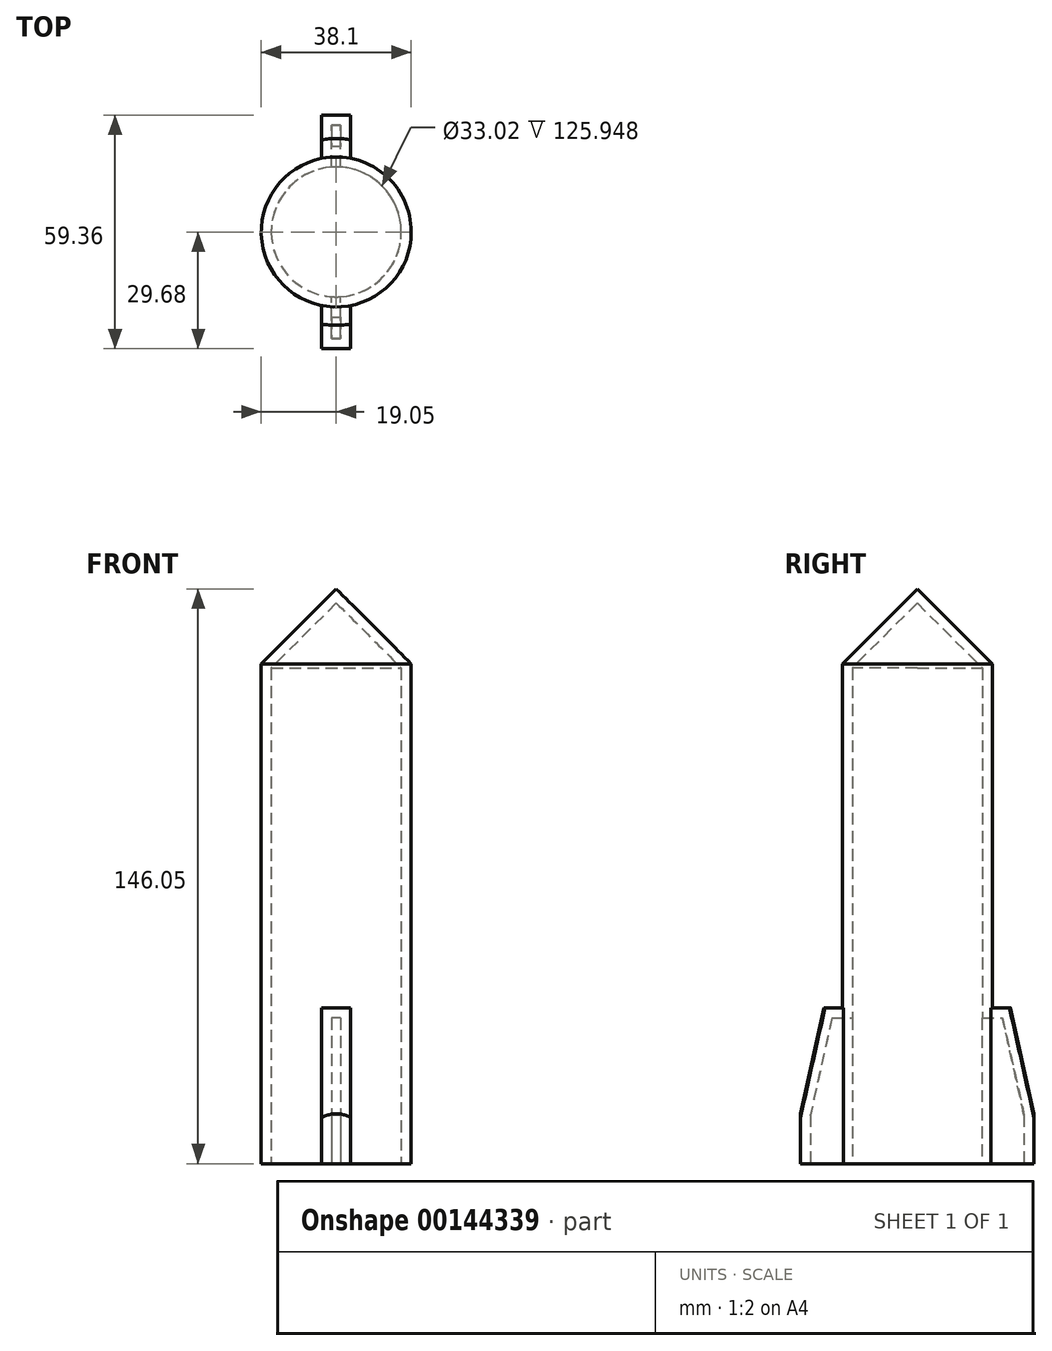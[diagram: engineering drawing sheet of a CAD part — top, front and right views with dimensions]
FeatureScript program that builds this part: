
annotation { "Feature Type Name" : "Feature", "Feature Type Description" : "" }
export const myFeature = defineFeature(function(context is Context, id is Id, definition is map)
    precondition{}
    {
        {
            var Q0;
            Q0=qCreatedBy(makeId("Top.planeOp"),FACE);
            var sketch = newSketch(context, id + "F0", { "sketchPlane" : qUnion([Q0])});
            skCircle(sketch, "E0", {"center": v(0, 0) * mm, "radius": 19.05 * mm});
            skSolve(sketch);
        }
        {
            var Q0;
            Q0 = qSketchRegion(id + "F0", true);
            extrude(context, id + "F1", {"entities" : qUnion([Q0]), "depth" : 127 * mm});
        }
        {
            var Q0;
            Q0=makeQuery(id+"F1.opExtrude","CAP_FACE",FACE,{"disambiguationData":[OSD([sQuery(id+"F0.wireOp",EDGE,"E0")])],"isStart":false});
            var sketch = newSketch(context, id + "F2", { "sketchPlane" : qUnion([Q0])});
            skCircle(sketch, "E1.0", {"center": v(0, 0) * mm, "radius": 19.05 * mm});
            skSolve(sketch);
        }
        {
            var Q0;
            Q0 = qSketchRegion(id + "F2", true);
            extrude(context, id + "F3", {"entities" : qUnion([Q0]), "operationType" : NewBodyOperationType.ADD, "depth" : 25.4 * mm, "hasDraft" : true, "draftAngle" : 45 * degree, "draftPullDirection" : true});
        }
        {
            var Q0;
            Q0=makeQuery(id+"F1.opExtrude","CAP_FACE",FACE,{"disambiguationData":[OSD([sQuery(id+"F0.wireOp",EDGE,"E0")])],"isStart":true});
            var sketch = newSketch(context, id + "F4", { "sketchPlane" : qUnion([Q0])});
            skLineSegment(sketch, "E2.bottom", {"start": v(3.69, 29.68) * mm, "end": v(-3.69, 29.68) * mm});
            skLineSegment(sketch, "E2.top", {"start": v(3.69, -29.68) * mm, "end": v(-3.69, -29.68) * mm});
            skLineSegment(sketch, "E2.left", {"start": v(3.69, 29.68) * mm, "end": v(3.69, -29.68) * mm});
            skLineSegment(sketch, "E2.right", {"start": v(-3.69, 29.68) * mm, "end": v(-3.69, -29.68) * mm});
            skPoint(sketch, "E2.middle", {"position": v(0, 0) * mm});
            skSolve(sketch);
        }
        {
            var Q0;
            Q0 = qSketchRegion(id + "F4", true);
            extrude(context, id + "F5", {"entities" : qUnion([Q0]), "operationType" : NewBodyOperationType.ADD, "oppositeDirection" : true, "depth" : 39.6 * mm});
        }
        {
            var Q0;
            Q0=qCreatedBy(makeId("Right.planeOp"),FACE);
            var sketch = newSketch(context, id + "F6", { "sketchPlane" : qUnion([Q0])});
            skLineSegment(sketch, "E3", {"start": v(22.65, 44.43) * mm, "end": v(32.5, 0) * mm});
            skLineSegment(sketch, "E4", {"start": v(32.5, 0) * mm, "end": v(32.5, 45.05) * mm});
            skLineSegment(sketch, "E5", {"start": v(32.5, 45.05) * mm, "end": v(22.65, 44.43) * mm});
            skLineSegment(sketch, "E6", {"start": v(0, 0) * mm, "end": v(0, -17.85) * mm, "construction": true});
            skSolve(sketch);
        }
        {
            var Q0;
            Q0=makeQuery(id+"F6.imprint","IMPRINT",FACE,{"disambiguationData":[TD([[makeQuery(id+"F6.imprint","IMPRINT",EDGE,{"derivedFrom":sQuery(id+"F6.wireOp",EDGE,"E3")}),1.0]])]});
            var Q1;
            Q1=sQuery(id+"F6.wireOp",EDGE,"E6");
            revolve(context, id + "F7", {"operationType" : NewBodyOperationType.REMOVE, "entities" : qUnion([Q0]), "axis" : qUnion([Q1]), "revolveType" : RevolveType.FULL, "oppositeDirection" : true});
        }
        {
            var Q0;
            Q0=makeQuery(id+"F5.boolean.opBoolean","MERGE",FACE,{"derivedFrom":[makeQuery(id+"F1.opExtrude","CAP_FACE",FACE,{"disambiguationData":[OSD([sQuery(id+"F0.wireOp",EDGE,"E0")])],"isStart":true}),makeQuery(id+"F5.opExtrude","CAP_FACE",FACE,{"disambiguationData":[OSD([sQuery(id+"F4.wireOp",EDGE,"E2.bottom"),sQuery(id+"F4.wireOp",EDGE,"E2.top"),sQuery(id+"F4.wireOp",EDGE,"E2.left"),sQuery(id+"F4.wireOp",EDGE,"E2.right")])],"isStart":true})]});
            var sketch = newSketch(context, id + "F8", { "sketchPlane" : qUnion([Q0])});
            skCircle(sketch, "E7", {"center": v(0, 0) * mm, "radius": 12.7 * mm});
            skSolve(sketch);
        }
        {
            var Q0;
            Q0=makeQuery(id+"F5.boolean.opBoolean","MERGE",FACE,{"derivedFrom":[makeQuery(id+"F1.opExtrude","CAP_FACE",FACE,{"disambiguationData":[OSD([sQuery(id+"F0.wireOp",EDGE,"E0")])],"isStart":true}),makeQuery(id+"F5.opExtrude","CAP_FACE",FACE,{"disambiguationData":[OSD([sQuery(id+"F4.wireOp",EDGE,"E2.bottom"),sQuery(id+"F4.wireOp",EDGE,"E2.top"),sQuery(id+"F4.wireOp",EDGE,"E2.left"),sQuery(id+"F4.wireOp",EDGE,"E2.right")])],"isStart":true})]});
            shell(context, id + "F9", {"entities" : qUnion([Q0]), "thickness" : 2.54 * mm});
        }
    });
